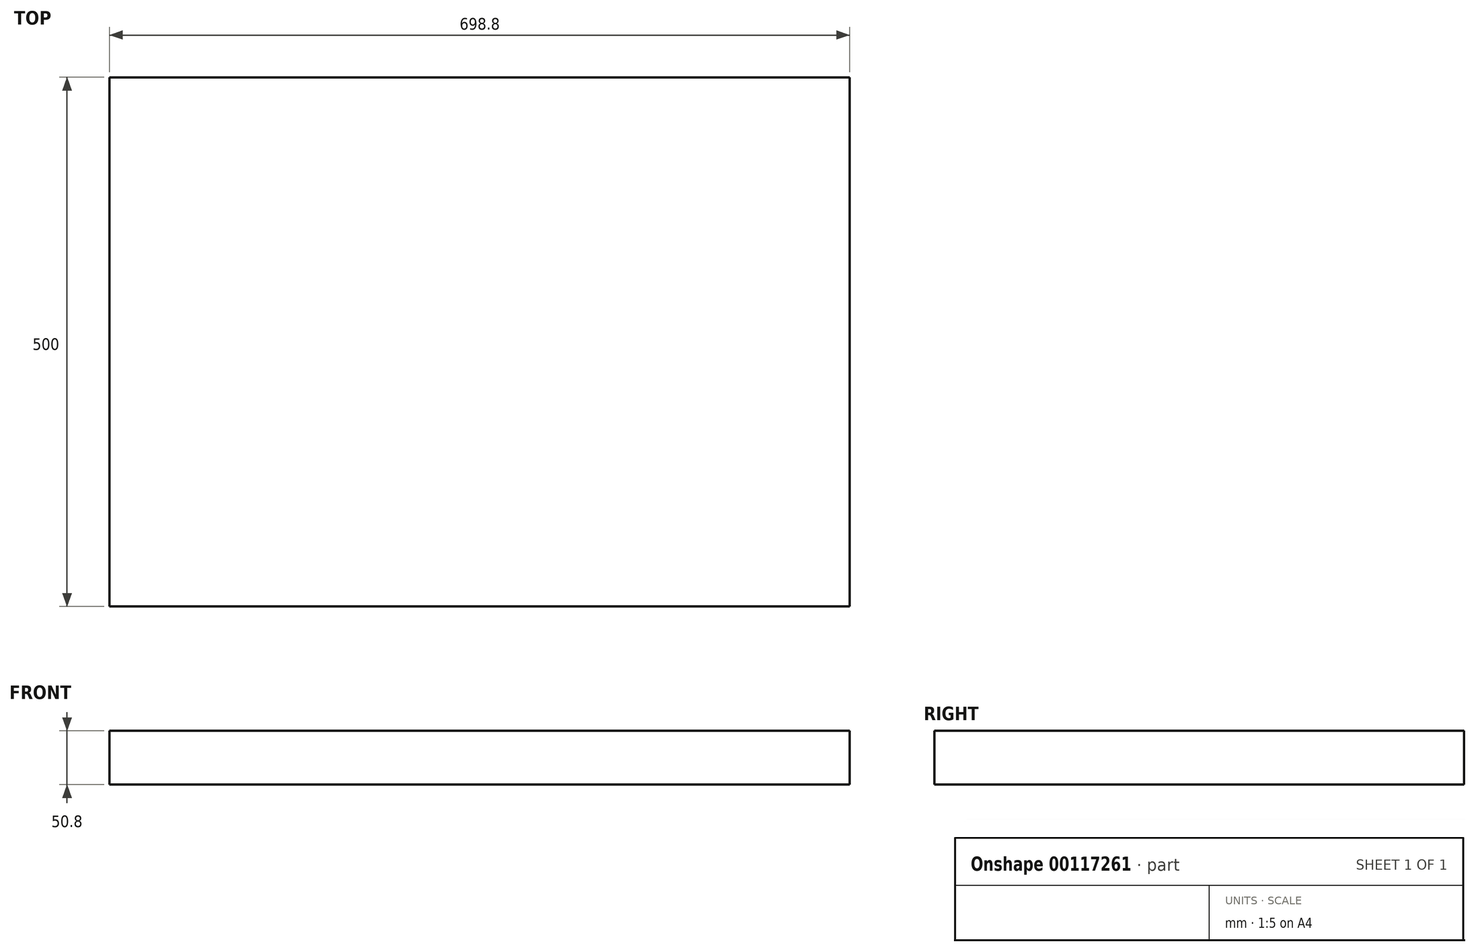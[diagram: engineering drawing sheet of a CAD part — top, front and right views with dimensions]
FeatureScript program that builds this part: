
annotation { "Feature Type Name" : "Feature", "Feature Type Description" : "" }
export const myFeature = defineFeature(function(context is Context, id is Id, definition is map)
    precondition{}
    {
        {
            var Q0;
            Q0=qCreatedBy(makeId("Top.planeOp"),FACE);
            var sketch = newSketch(context, id + "F0", { "sketchPlane" : qUnion([Q0])});
            skLineSegment(sketch, "E0.bottom", {"start": v(-374, 193.53) * mm, "end": v(324.8, 193.53) * mm});
            skLineSegment(sketch, "E0.top", {"start": v(-374, -306.47) * mm, "end": v(324.8, -306.47) * mm});
            skLineSegment(sketch, "E0.left", {"start": v(-374, 193.53) * mm, "end": v(-374, -306.47) * mm});
            skLineSegment(sketch, "E0.right", {"start": v(324.8, 193.53) * mm, "end": v(324.8, -306.47) * mm});
            skSolve(sketch);
        }
        {
            var Q0;
            Q0=makeQuery(id+"F0.imprint","IMPRINT",FACE,{"disambiguationData":[TD([[makeQuery(id+"F0.imprint","IMPRINT",EDGE,{"derivedFrom":sQuery(id+"F0.wireOp",EDGE,"E0.bottom")}),-1.0]])]});
            extrude(context, id + "F1", {"entities" : qUnion([Q0]), "oppositeDirection" : true, "depth" : 50.8 * mm, "offsetDistance" : 25 * mm});
        }
    });
